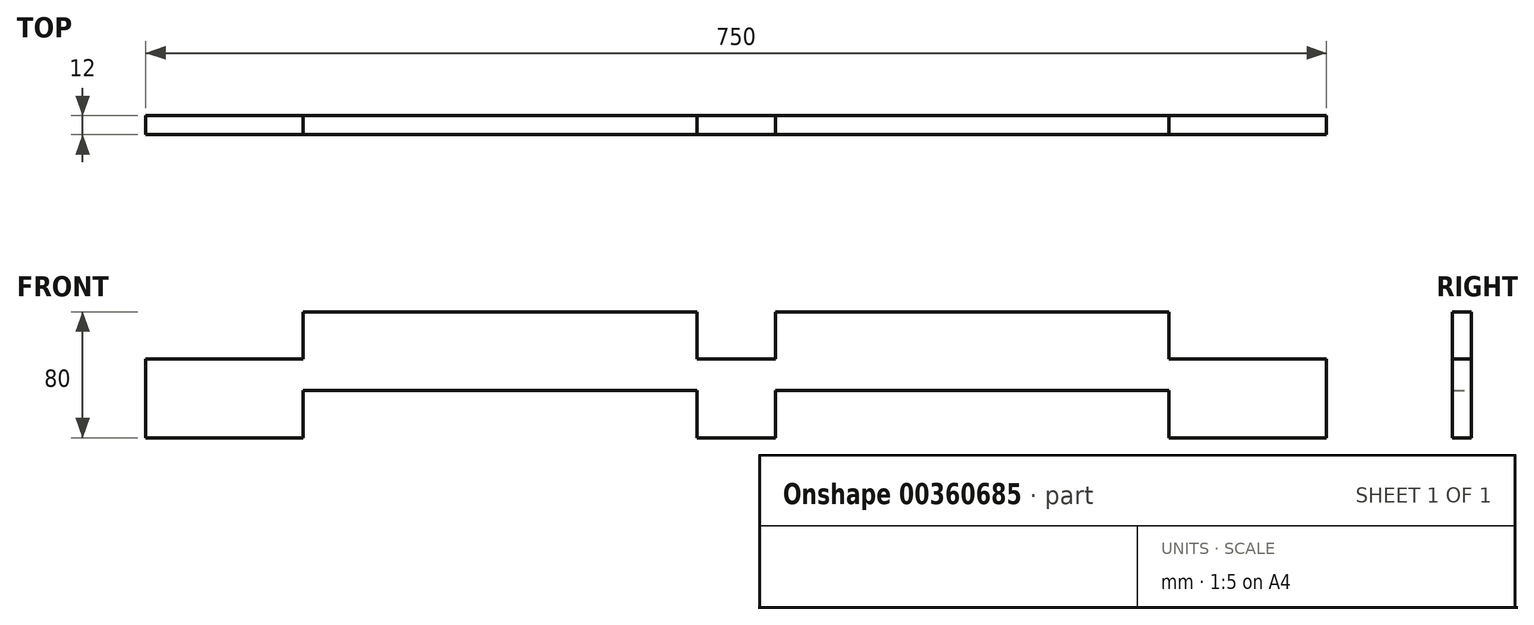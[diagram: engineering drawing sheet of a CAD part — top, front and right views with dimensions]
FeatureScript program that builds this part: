
annotation { "Feature Type Name" : "Feature", "Feature Type Description" : "" }
export const myFeature = defineFeature(function(context is Context, id is Id, definition is map)
    precondition{}
    {
        {
            var Q0;
            Q0=qCreatedBy(makeId("Front.planeOp"),FACE);
            var sketch = newSketch(context, id + "F0", { "sketchPlane" : qUnion([Q0])});
            skLineSegment(sketch, "E0.bottom", {"start": v(0, 0) * mm, "end": v(100, 0) * mm});
            skLineSegment(sketch, "E0.top", {"start": v(0, 50) * mm, "end": v(100, 50) * mm});
            skLineSegment(sketch, "E0.left", {"start": v(0, 0) * mm, "end": v(0, 50) * mm});
            skLineSegment(sketch, "E0.right", {"start": v(750, 0) * mm, "end": v(750, 50) * mm});
            skLineSegment(sketch, "E1.top", {"start": v(100, 80) * mm, "end": v(350, 80) * mm});
            skLineSegment(sketch, "E1.left", {"start": v(100, 50) * mm, "end": v(100, 80) * mm});
            skLineSegment(sketch, "E1.right", {"start": v(350, 50) * mm, "end": v(350, 80) * mm});
            skLineSegment(sketch, "E2.top", {"start": v(400, 80) * mm, "end": v(650, 80) * mm});
            skLineSegment(sketch, "E2.left", {"start": v(400, 50) * mm, "end": v(400, 80) * mm});
            skLineSegment(sketch, "E2.right", {"start": v(650, 50) * mm, "end": v(650, 80) * mm});
            skLineSegment(sketch, "E3.trimOffspring", {"start": v(350, 50) * mm, "end": v(400, 50) * mm});
            skLineSegment(sketch, "E4.trimOffspring", {"start": v(650, 50) * mm, "end": v(750, 50) * mm});
            skLineSegment(sketch, "E5.top", {"start": v(100, 30) * mm, "end": v(350, 30) * mm});
            skLineSegment(sketch, "E5.left", {"start": v(100, 0) * mm, "end": v(100, 30) * mm});
            skLineSegment(sketch, "E5.right", {"start": v(350, 0) * mm, "end": v(350, 30) * mm});
            skLineSegment(sketch, "E6.top", {"start": v(400, 30) * mm, "end": v(650, 30) * mm});
            skLineSegment(sketch, "E6.left", {"start": v(400, 0) * mm, "end": v(400, 30) * mm});
            skLineSegment(sketch, "E6.right", {"start": v(650, 0) * mm, "end": v(650, 30) * mm});
            skLineSegment(sketch, "E7.trimOffspring", {"start": v(350, 0) * mm, "end": v(400, 0) * mm});
            skLineSegment(sketch, "E8.trimOffspring", {"start": v(650, 0) * mm, "end": v(750, 0) * mm});
            skSolve(sketch);
        }
        {
            var Q0;
            Q0=makeQuery(id+"F0.imprint","IMPRINT",FACE,{"disambiguationData":[TD([[makeQuery(id+"F0.imprint","IMPRINT",EDGE,{"derivedFrom":sQuery(id+"F0.wireOp",EDGE,"E0.bottom")}),1.0]])]});
            extrude(context, id + "F1", {"entities" : qUnion([Q0]), "depth" : 12 * mm});
        }
    });
